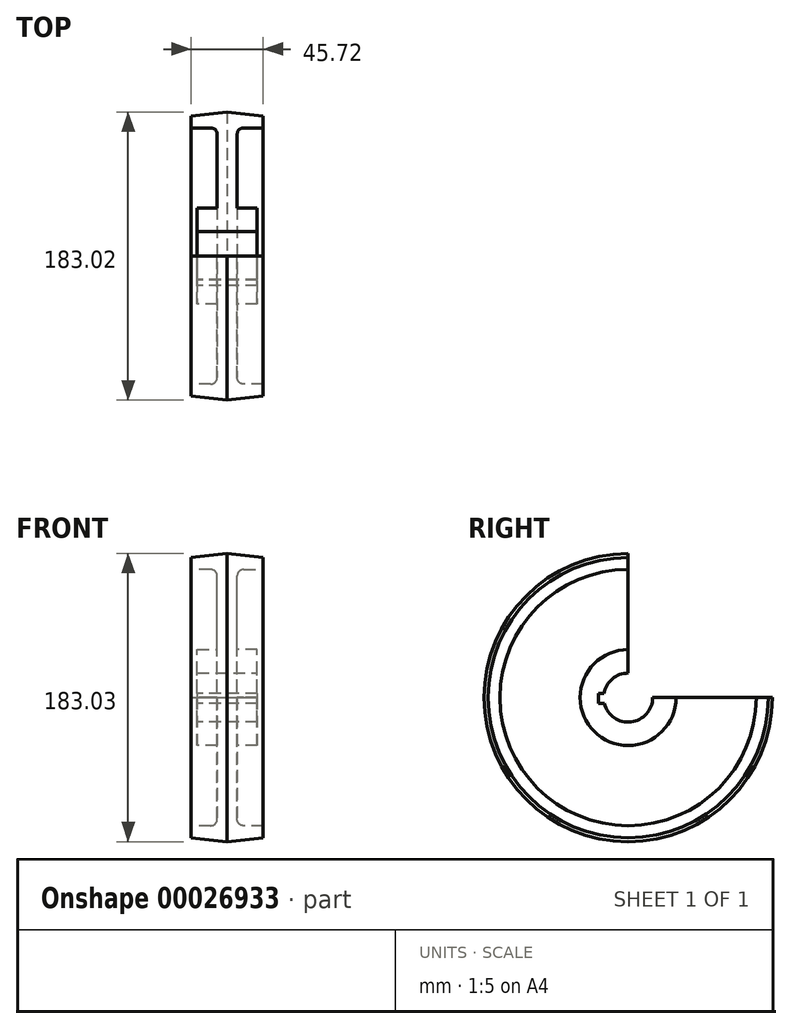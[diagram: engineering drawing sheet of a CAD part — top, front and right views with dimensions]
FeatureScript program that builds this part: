
annotation { "Feature Type Name" : "Feature", "Feature Type Description" : "" }
export const myFeature = defineFeature(function(context is Context, id is Id, definition is map)
    precondition{}
    {
        {
            var Q0;
            Q0=qCreatedBy(makeId("Front.planeOp"),FACE);
            var sketch = newSketch(context, id + "F0", { "sketchPlane" : qUnion([Q0])});
            skLineSegment(sketch, "E0", {"start": v(0, 0) * mm, "end": v(38.1, 0) * mm});
            skLineSegment(sketch, "E1", {"start": v(38.1, 0) * mm, "end": v(38.1, 14.92) * mm});
            skLineSegment(sketch, "E2", {"start": v(38.1, 14.92) * mm, "end": v(25.4, 14.92) * mm});
            skLineSegment(sketch, "E3", {"start": v(25.4, 14.92) * mm, "end": v(25.4, 61.73) * mm});
            skLineSegment(sketch, "E4", {"start": v(29.46, 65.8) * mm, "end": v(41.91, 65.8) * mm});
            skLineSegment(sketch, "E5", {"start": v(41.91, 65.8) * mm, "end": v(41.91, 73.42) * mm});
            skLineSegment(sketch, "E6", {"start": v(0, 0) * mm, "end": v(0, 14.92) * mm});
            skLineSegment(sketch, "E7", {"start": v(0, 14.92) * mm, "end": v(12.7, 14.92) * mm});
            skLineSegment(sketch, "E8", {"start": v(12.7, 14.92) * mm, "end": v(12.7, 61.73) * mm});
            skLineSegment(sketch, "E9", {"start": v(8.64, 65.8) * mm, "end": v(-3.81, 65.8) * mm});
            skLineSegment(sketch, "E10", {"start": v(-3.81, 65.8) * mm, "end": v(-3.81, 73.42) * mm});
            skLineSegment(sketch, "E11", {"start": v(19.05, 75.96) * mm, "end": v(41.91, 73.42) * mm});
            skLineSegment(sketch, "E12", {"start": v(-3.81, 73.42) * mm, "end": v(19.05, 75.96) * mm});
            skLineSegment(sketch, "E13", {"start": v(0, -15.56) * mm, "end": v(38.1, -15.56) * mm});
            skPoint(sketch, "E14.visualSharp", {"position": v(12.7, 65.8) * mm});
            skArc(sketch, "E14.filletArc", {"start": v(12.7, 61.73) * mm, "mid": v(11.5, 64.6) * mm, "end": v(8.64, 65.8) * mm});
            skPoint(sketch, "E15.visualSharp", {"position": v(25.4, 65.8) * mm});
            skArc(sketch, "E15.filletArc", {"start": v(29.46, 65.8) * mm, "mid": v(26.6, 64.6) * mm, "end": v(25.4, 61.73) * mm});
            skSolve(sketch);
        }
        {
            var Q0;
            Q0 = qSketchRegion(id + "F0", true);
            var Q1;
            Q1=sQuery(id+"F0.wireOp",EDGE,"E13");
            revolve(context, id + "F1", {"entities" : qUnion([Q0]), "axis" : qUnion([Q1]), "revolveType" : RevolveType.ONE_DIRECTION, "angle" : 270 * degree});
        }
        {
            var Q0;
            Q0=makeQuery(id+"F1.opRevolve","SWEPT_FACE",FACE,{"disambiguationData":[OSD([sQuery(id+"F0.wireOp",EDGE,"E6")])]});
            var sketch = newSketch(context, id + "F2", { "sketchPlane" : qUnion([Q0])});
            skLineSegment(sketch, "E16.rect.bottom", {"start": v(18.72, -12.9) * mm, "end": v(12.37, -12.9) * mm});
            skLineSegment(sketch, "E16.rect.top", {"start": v(18.72, -19.25) * mm, "end": v(12.37, -19.25) * mm});
            skLineSegment(sketch, "E16.rect.left", {"start": v(18.72, -12.9) * mm, "end": v(18.72, -19.25) * mm});
            skLineSegment(sketch, "E16.rect.right", {"start": v(12.37, -12.9) * mm, "end": v(12.37, -19.25) * mm});
            skPoint(sketch, "E16.rect.middle", {"position": v(15.55, -16.08) * mm});
            skSolve(sketch);
        }
        {
            var Q0;
            {var subQ5=sQuery(id+"F2.wireOp",EDGE,"E16.rect.left");Q0=makeQuery(id+"F2.imprint","IMPRINT",FACE,{"disambiguationData":[TD([[makeQuery(id+"F2.imprint","IMPRINT",EDGE,{"derivedFrom":subQ5}),-1.0]])]});}
            extrude(context, id + "F3", {"entities" : qUnion([Q0]), "operationType" : NewBodyOperationType.REMOVE, "endBound" : BoundingType.THROUGH_ALL, "oppositeDirection" : true, "depth" : 25.4 * mm});
        }
    });
